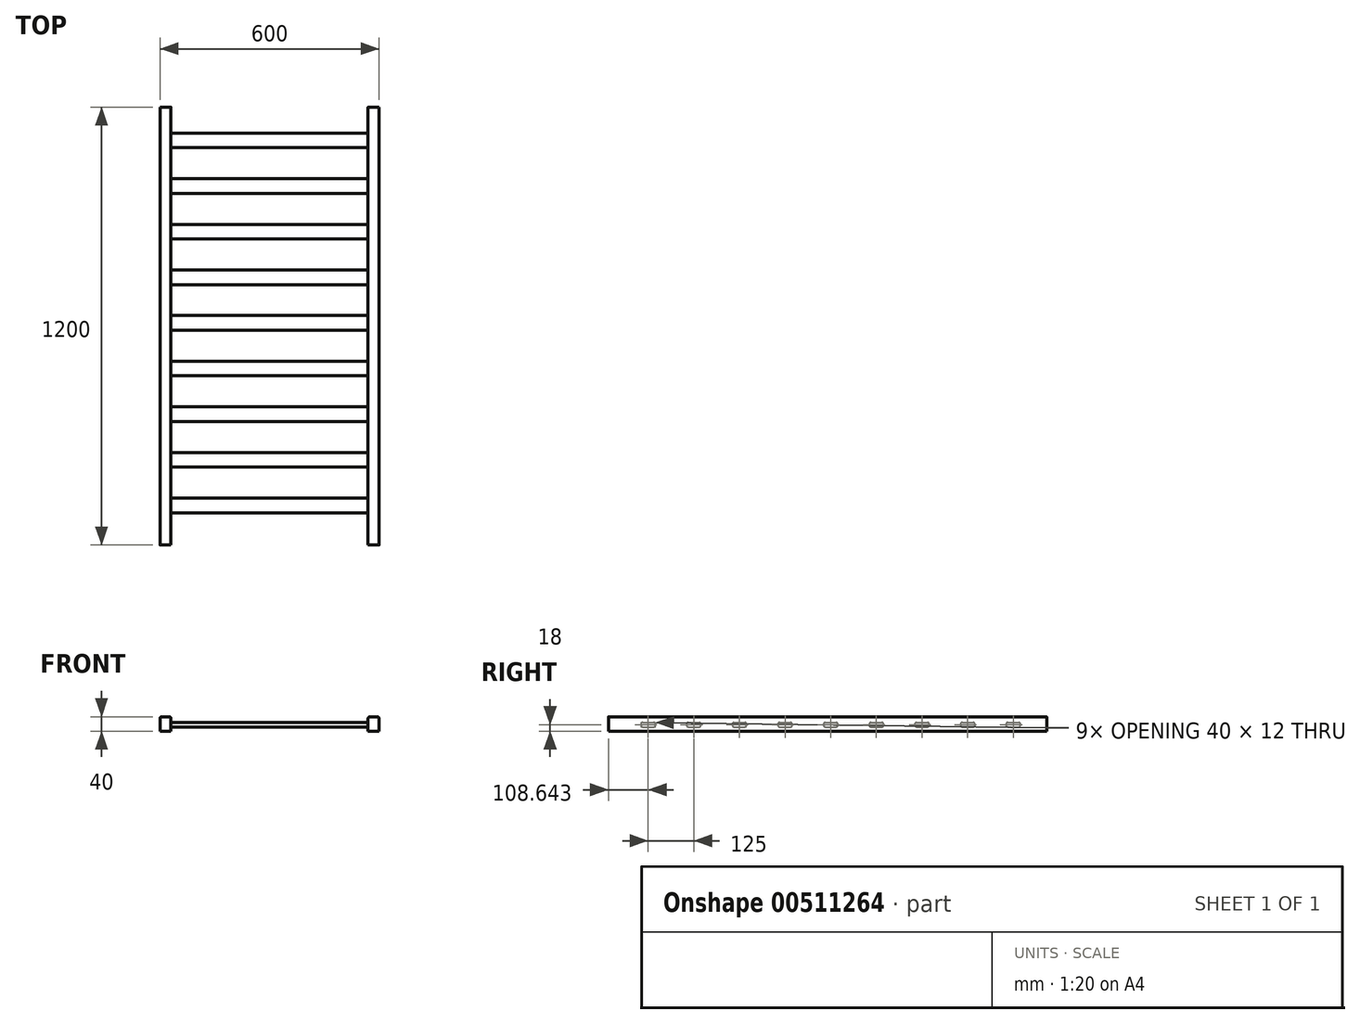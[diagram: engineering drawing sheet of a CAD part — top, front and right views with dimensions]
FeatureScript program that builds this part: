
annotation { "Feature Type Name" : "Feature", "Feature Type Description" : "" }
export const myFeature = defineFeature(function(context is Context, id is Id, definition is map)
    precondition{}
    {
        {
            var Q0;
            Q0=qCreatedBy(makeId("Front.planeOp"),FACE);
            var sketch = newSketch(context, id + "F0", { "sketchPlane" : qUnion([Q0])});
            skLineSegment(sketch, "E0.bottom", {"start": v(-334.17, 0) * mm, "end": v(-314.17, 0) * mm});
            skLineSegment(sketch, "E0.top", {"start": v(-339.17, -40) * mm, "end": v(-309.17, -40) * mm});
            skLineSegment(sketch, "E0.left", {"start": v(-339.17, -5) * mm, "end": v(-339.17, -40) * mm});
            skLineSegment(sketch, "E0.right", {"start": v(-309.17, -5) * mm, "end": v(-309.17, -40) * mm});
            skPoint(sketch, "E1.visualSharp", {"position": v(-339.17, 0) * mm});
            skArc(sketch, "E1.filletArc", {"start": v(-334.17, 0) * mm, "mid": v(-337.7, -1.46) * mm, "end": v(-339.17, -5) * mm});
            skPoint(sketch, "E2.visualSharp", {"position": v(-309.17, 0) * mm});
            skArc(sketch, "E2.filletArc", {"start": v(-309.17, -5) * mm, "mid": v(-310.63, -1.46) * mm, "end": v(-314.17, 0) * mm});
            skSolve(sketch);
        }
        {
            var Q0;
            Q0=qSketchRegion(id+"F0",true);
            extrude(context, id + "F1", {"entities" : qUnion([Q0]), "depth" : 1200 * mm});
        }
        {
            var Q0;
            Q0=makeQuery(id+"F1.opExtrude","SWEPT_FACE",FACE,{"disambiguationData":[OSD([sQuery(id+"F0.wireOp",EDGE,"E0.right")])]});
            var sketch = newSketch(context, id + "F2", { "sketchPlane" : qUnion([Q0])});
            skLineSegment(sketch, "E3.bottom", {"start": v(-1106.36, -16) * mm, "end": v(-1076.36, -16) * mm});
            skLineSegment(sketch, "E3.top", {"start": v(-1106.36, -28) * mm, "end": v(-1076.36, -28) * mm});
            skLineSegment(sketch, "E3.left", {"start": v(-1111.36, -21) * mm, "end": v(-1111.36, -23) * mm});
            skLineSegment(sketch, "E3.right", {"start": v(-1071.36, -21) * mm, "end": v(-1071.36, -23) * mm});
            skPoint(sketch, "E4.visualSharp", {"position": v(-1111.36, -16) * mm});
            skArc(sketch, "E4.filletArc", {"start": v(-1106.36, -16) * mm, "mid": v(-1109.9, -17.46) * mm, "end": v(-1111.36, -21) * mm});
            skPoint(sketch, "E5.visualSharp", {"position": v(-1071.36, -16) * mm});
            skArc(sketch, "E5.filletArc", {"start": v(-1071.36, -21) * mm, "mid": v(-1072.82, -17.46) * mm, "end": v(-1076.36, -16) * mm});
            skPoint(sketch, "E6.visualSharp", {"position": v(-1071.36, -28) * mm});
            skArc(sketch, "E6.filletArc", {"start": v(-1076.36, -28) * mm, "mid": v(-1072.82, -26.54) * mm, "end": v(-1071.36, -23) * mm});
            skPoint(sketch, "E7.visualSharp", {"position": v(-1111.36, -28) * mm});
            skArc(sketch, "E7.filletArc", {"start": v(-1111.36, -23) * mm, "mid": v(-1109.9, -26.54) * mm, "end": v(-1106.36, -28) * mm});
            skArc(sketch, "E8.1.0.0", {"start": v(-946.36, -21) * mm, "mid": v(-947.82, -17.46) * mm, "end": v(-951.36, -16) * mm});
            skLineSegment(sketch, "E8.1.0.1", {"start": v(-946.36, -21) * mm, "end": v(-946.36, -23) * mm});
            skArc(sketch, "E8.1.0.2", {"start": v(-951.36, -28) * mm, "mid": v(-947.82, -26.54) * mm, "end": v(-946.36, -23) * mm});
            skLineSegment(sketch, "E8.1.0.3", {"start": v(-981.36, -28) * mm, "end": v(-951.36, -28) * mm});
            skLineSegment(sketch, "E8.1.0.4", {"start": v(-981.36, -16) * mm, "end": v(-951.36, -16) * mm});
            skArc(sketch, "E8.1.0.5", {"start": v(-981.36, -16) * mm, "mid": v(-984.9, -17.46) * mm, "end": v(-986.36, -21) * mm});
            skLineSegment(sketch, "E8.1.0.6", {"start": v(-986.36, -21) * mm, "end": v(-986.36, -23) * mm});
            skArc(sketch, "E8.1.0.7", {"start": v(-986.36, -23) * mm, "mid": v(-984.9, -26.54) * mm, "end": v(-981.36, -28) * mm});
            skArc(sketch, "E8.2.0.0", {"start": v(-821.36, -21) * mm, "mid": v(-822.82, -17.46) * mm, "end": v(-826.36, -16) * mm});
            skLineSegment(sketch, "E8.2.0.1", {"start": v(-821.36, -21) * mm, "end": v(-821.36, -23) * mm});
            skArc(sketch, "E8.2.0.2", {"start": v(-826.36, -28) * mm, "mid": v(-822.82, -26.54) * mm, "end": v(-821.36, -23) * mm});
            skLineSegment(sketch, "E8.2.0.3", {"start": v(-856.36, -28) * mm, "end": v(-826.36, -28) * mm});
            skLineSegment(sketch, "E8.2.0.4", {"start": v(-856.36, -16) * mm, "end": v(-826.36, -16) * mm});
            skArc(sketch, "E8.2.0.5", {"start": v(-856.36, -16) * mm, "mid": v(-859.9, -17.46) * mm, "end": v(-861.36, -21) * mm});
            skLineSegment(sketch, "E8.2.0.6", {"start": v(-861.36, -21) * mm, "end": v(-861.36, -23) * mm});
            skArc(sketch, "E8.2.0.7", {"start": v(-861.36, -23) * mm, "mid": v(-859.9, -26.54) * mm, "end": v(-856.36, -28) * mm});
            skArc(sketch, "E8.3.0.0", {"start": v(-696.36, -21) * mm, "mid": v(-697.82, -17.46) * mm, "end": v(-701.36, -16) * mm});
            skLineSegment(sketch, "E8.3.0.1", {"start": v(-696.36, -21) * mm, "end": v(-696.36, -23) * mm});
            skArc(sketch, "E8.3.0.2", {"start": v(-701.36, -28) * mm, "mid": v(-697.82, -26.54) * mm, "end": v(-696.36, -23) * mm});
            skLineSegment(sketch, "E8.3.0.3", {"start": v(-731.36, -28) * mm, "end": v(-701.36, -28) * mm});
            skLineSegment(sketch, "E8.3.0.4", {"start": v(-731.36, -16) * mm, "end": v(-701.36, -16) * mm});
            skArc(sketch, "E8.3.0.5", {"start": v(-731.36, -16) * mm, "mid": v(-734.9, -17.46) * mm, "end": v(-736.36, -21) * mm});
            skLineSegment(sketch, "E8.3.0.6", {"start": v(-736.36, -21) * mm, "end": v(-736.36, -23) * mm});
            skArc(sketch, "E8.3.0.7", {"start": v(-736.36, -23) * mm, "mid": v(-734.9, -26.54) * mm, "end": v(-731.36, -28) * mm});
            skArc(sketch, "E8.4.0.0", {"start": v(-571.36, -21) * mm, "mid": v(-572.82, -17.46) * mm, "end": v(-576.36, -16) * mm});
            skLineSegment(sketch, "E8.4.0.1", {"start": v(-571.36, -21) * mm, "end": v(-571.36, -23) * mm});
            skArc(sketch, "E8.4.0.2", {"start": v(-576.36, -28) * mm, "mid": v(-572.82, -26.54) * mm, "end": v(-571.36, -23) * mm});
            skLineSegment(sketch, "E8.4.0.3", {"start": v(-606.36, -28) * mm, "end": v(-576.36, -28) * mm});
            skLineSegment(sketch, "E8.4.0.4", {"start": v(-606.36, -16) * mm, "end": v(-576.36, -16) * mm});
            skArc(sketch, "E8.4.0.5", {"start": v(-606.36, -16) * mm, "mid": v(-609.9, -17.46) * mm, "end": v(-611.36, -21) * mm});
            skLineSegment(sketch, "E8.4.0.6", {"start": v(-611.36, -21) * mm, "end": v(-611.36, -23) * mm});
            skArc(sketch, "E8.4.0.7", {"start": v(-611.36, -23) * mm, "mid": v(-609.9, -26.54) * mm, "end": v(-606.36, -28) * mm});
            skArc(sketch, "E8.5.0.0", {"start": v(-446.36, -21) * mm, "mid": v(-447.82, -17.46) * mm, "end": v(-451.36, -16) * mm});
            skLineSegment(sketch, "E8.5.0.1", {"start": v(-446.36, -21) * mm, "end": v(-446.36, -23) * mm});
            skArc(sketch, "E8.5.0.2", {"start": v(-451.36, -28) * mm, "mid": v(-447.82, -26.54) * mm, "end": v(-446.36, -23) * mm});
            skLineSegment(sketch, "E8.5.0.3", {"start": v(-481.36, -28) * mm, "end": v(-451.36, -28) * mm});
            skLineSegment(sketch, "E8.5.0.4", {"start": v(-481.36, -16) * mm, "end": v(-451.36, -16) * mm});
            skArc(sketch, "E8.5.0.5", {"start": v(-481.36, -16) * mm, "mid": v(-484.9, -17.46) * mm, "end": v(-486.36, -21) * mm});
            skLineSegment(sketch, "E8.5.0.6", {"start": v(-486.36, -21) * mm, "end": v(-486.36, -23) * mm});
            skArc(sketch, "E8.5.0.7", {"start": v(-486.36, -23) * mm, "mid": v(-484.9, -26.54) * mm, "end": v(-481.36, -28) * mm});
            skArc(sketch, "E8.6.0.0", {"start": v(-321.36, -21) * mm, "mid": v(-322.82, -17.46) * mm, "end": v(-326.36, -16) * mm});
            skLineSegment(sketch, "E8.6.0.1", {"start": v(-321.36, -21) * mm, "end": v(-321.36, -23) * mm});
            skArc(sketch, "E8.6.0.2", {"start": v(-326.36, -28) * mm, "mid": v(-322.82, -26.54) * mm, "end": v(-321.36, -23) * mm});
            skLineSegment(sketch, "E8.6.0.3", {"start": v(-356.36, -28) * mm, "end": v(-326.36, -28) * mm});
            skLineSegment(sketch, "E8.6.0.4", {"start": v(-356.36, -16) * mm, "end": v(-326.36, -16) * mm});
            skArc(sketch, "E8.6.0.5", {"start": v(-356.36, -16) * mm, "mid": v(-359.9, -17.46) * mm, "end": v(-361.36, -21) * mm});
            skLineSegment(sketch, "E8.6.0.6", {"start": v(-361.36, -21) * mm, "end": v(-361.36, -23) * mm});
            skArc(sketch, "E8.6.0.7", {"start": v(-361.36, -23) * mm, "mid": v(-359.9, -26.54) * mm, "end": v(-356.36, -28) * mm});
            skArc(sketch, "E8.7.0.0", {"start": v(-196.36, -21) * mm, "mid": v(-197.82, -17.46) * mm, "end": v(-201.36, -16) * mm});
            skLineSegment(sketch, "E8.7.0.1", {"start": v(-196.36, -21) * mm, "end": v(-196.36, -23) * mm});
            skArc(sketch, "E8.7.0.2", {"start": v(-201.36, -28) * mm, "mid": v(-197.82, -26.54) * mm, "end": v(-196.36, -23) * mm});
            skLineSegment(sketch, "E8.7.0.3", {"start": v(-231.36, -28) * mm, "end": v(-201.36, -28) * mm});
            skLineSegment(sketch, "E8.7.0.4", {"start": v(-231.36, -16) * mm, "end": v(-201.36, -16) * mm});
            skArc(sketch, "E8.7.0.5", {"start": v(-231.36, -16) * mm, "mid": v(-234.9, -17.46) * mm, "end": v(-236.36, -21) * mm});
            skLineSegment(sketch, "E8.7.0.6", {"start": v(-236.36, -21) * mm, "end": v(-236.36, -23) * mm});
            skArc(sketch, "E8.7.0.7", {"start": v(-236.36, -23) * mm, "mid": v(-234.9, -26.54) * mm, "end": v(-231.36, -28) * mm});
            skArc(sketch, "E8.8.0.0", {"start": v(-71.36, -21) * mm, "mid": v(-72.82, -17.46) * mm, "end": v(-76.36, -16) * mm});
            skLineSegment(sketch, "E8.8.0.1", {"start": v(-71.36, -21) * mm, "end": v(-71.36, -23) * mm});
            skArc(sketch, "E8.8.0.2", {"start": v(-76.36, -28) * mm, "mid": v(-72.82, -26.54) * mm, "end": v(-71.36, -23) * mm});
            skLineSegment(sketch, "E8.8.0.3", {"start": v(-106.36, -28) * mm, "end": v(-76.36, -28) * mm});
            skLineSegment(sketch, "E8.8.0.4", {"start": v(-106.36, -16) * mm, "end": v(-76.36, -16) * mm});
            skArc(sketch, "E8.8.0.5", {"start": v(-106.36, -16) * mm, "mid": v(-109.9, -17.46) * mm, "end": v(-111.36, -21) * mm});
            skLineSegment(sketch, "E8.8.0.6", {"start": v(-111.36, -21) * mm, "end": v(-111.36, -23) * mm});
            skArc(sketch, "E8.8.0.7", {"start": v(-111.36, -23) * mm, "mid": v(-109.9, -26.54) * mm, "end": v(-106.36, -28) * mm});
            skLineSegment(sketch, "E8.direction1", {"start": v(-1076.36, -21) * mm, "end": v(-951.36, -21) * mm, "construction": true});
            skSolve(sketch);
        }
        {
            var Q0;
            Q0=makeQuery(id+"F2.imprint","IMPRINT",FACE,{"disambiguationData":[TD([[makeQuery(id+"F2.imprint","IMPRINT",EDGE,{"derivedFrom":sQuery(id+"F2.wireOp",EDGE,"E3.bottom")}),-1.0]])]});
            var Q1;
            Q1=makeQuery(id+"F2.imprint","IMPRINT",FACE,{"disambiguationData":[TD([[makeQuery(id+"F2.imprint","IMPRINT",EDGE,{"derivedFrom":sQuery(id+"F2.wireOp",EDGE,"E8.1.0.0")}),1.0]])]});
            var Q2;
            Q2=makeQuery(id+"F2.imprint","IMPRINT",FACE,{"disambiguationData":[TD([[makeQuery(id+"F2.imprint","IMPRINT",EDGE,{"derivedFrom":sQuery(id+"F2.wireOp",EDGE,"E8.2.0.0")}),1.0]])]});
            var Q3;
            Q3=makeQuery(id+"F2.imprint","IMPRINT",FACE,{"disambiguationData":[TD([[makeQuery(id+"F2.imprint","IMPRINT",EDGE,{"derivedFrom":sQuery(id+"F2.wireOp",EDGE,"E8.3.0.0")}),1.0]])]});
            var Q4;
            Q4=makeQuery(id+"F2.imprint","IMPRINT",FACE,{"disambiguationData":[TD([[makeQuery(id+"F2.imprint","IMPRINT",EDGE,{"derivedFrom":sQuery(id+"F2.wireOp",EDGE,"E8.4.0.0")}),1.0]])]});
            var Q5;
            Q5=makeQuery(id+"F2.imprint","IMPRINT",FACE,{"disambiguationData":[TD([[makeQuery(id+"F2.imprint","IMPRINT",EDGE,{"derivedFrom":sQuery(id+"F2.wireOp",EDGE,"E8.5.0.0")}),1.0]])]});
            var Q6;
            Q6=makeQuery(id+"F2.imprint","IMPRINT",FACE,{"disambiguationData":[TD([[makeQuery(id+"F2.imprint","IMPRINT",EDGE,{"derivedFrom":sQuery(id+"F2.wireOp",EDGE,"E8.6.0.0")}),1.0]])]});
            var Q7;
            Q7=makeQuery(id+"F2.imprint","IMPRINT",FACE,{"disambiguationData":[TD([[makeQuery(id+"F2.imprint","IMPRINT",EDGE,{"derivedFrom":sQuery(id+"F2.wireOp",EDGE,"E8.7.0.0")}),1.0]])]});
            var Q8;
            Q8=makeQuery(id+"F2.imprint","IMPRINT",FACE,{"disambiguationData":[TD([[makeQuery(id+"F2.imprint","IMPRINT",EDGE,{"derivedFrom":sQuery(id+"F2.wireOp",EDGE,"E8.8.0.0")}),1.0]])]});
            extrude(context, id + "F3", {"entities" : qUnion([Q0, Q1, Q2, Q3, Q4, Q5, Q6, Q7, Q8]), "operationType" : NewBodyOperationType.ADD, "depth" : 270 * mm});
        }
        {
            var Q0;
            Q0=makeQuery(id+"F1.opExtrude","SWEPT_BODY",BODY,{"disambiguationData":[OSD([sQuery(id+"F0.wireOp",EDGE,"E0.bottom"),sQuery(id+"F0.wireOp",EDGE,"E0.top"),sQuery(id+"F0.wireOp",EDGE,"E0.left"),sQuery(id+"F0.wireOp",EDGE,"E0.right"),sQuery(id+"F0.wireOp",EDGE,"E1.filletArc"),sQuery(id+"F0.wireOp",EDGE,"E2.filletArc")])]});
            var Q1;
            Q1=makeQuery(id+"F3.opExtrude","CAP_FACE",FACE,{"disambiguationData":[OSD([sQuery(id+"F2.wireOp",EDGE,"E8.2.0.0"),sQuery(id+"F2.wireOp",EDGE,"E8.2.0.1"),sQuery(id+"F2.wireOp",EDGE,"E8.2.0.2"),sQuery(id+"F2.wireOp",EDGE,"E8.2.0.3"),sQuery(id+"F2.wireOp",EDGE,"E8.2.0.4"),sQuery(id+"F2.wireOp",EDGE,"E8.2.0.5"),sQuery(id+"F2.wireOp",EDGE,"E8.2.0.6"),sQuery(id+"F2.wireOp",EDGE,"E8.2.0.7")])],"isStart":false});
            mirror(context, id + "F4", {"operationType" : NewBodyOperationType.ADD, "entities" : qUnion([Q0]), "mirrorPlane" : qUnion([Q1])});
        }
    });
